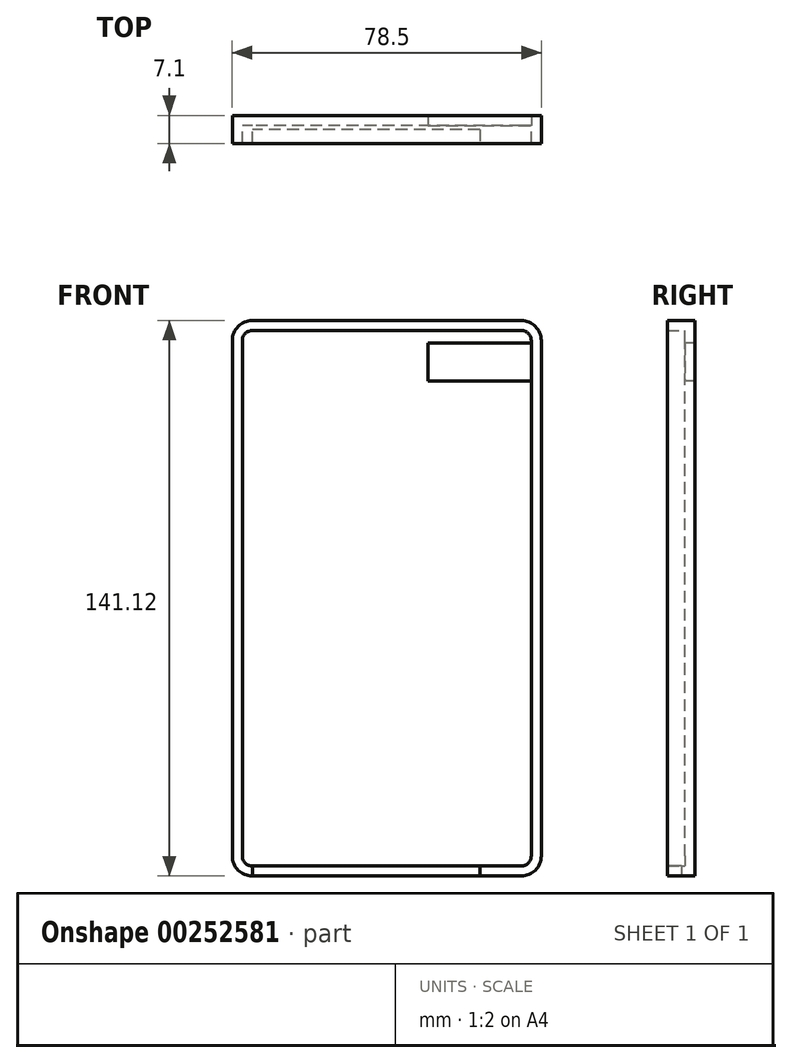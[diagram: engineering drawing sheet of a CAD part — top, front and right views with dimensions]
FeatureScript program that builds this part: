
annotation { "Feature Type Name" : "Feature", "Feature Type Description" : "" }
export const myFeature = defineFeature(function(context is Context, id is Id, definition is map)
    precondition{}
    {
        {
            var Q0;
            Q0=qCreatedBy(makeId("Front.planeOp"),FACE);
            var sketch = newSketch(context, id + "F0", { "sketchPlane" : qUnion([Q0])});
            skLineSegment(sketch, "E0.bottom", {"start": v(39.25, -70.56) * mm, "end": v(-39.25, -70.56) * mm});
            skLineSegment(sketch, "E0.top", {"start": v(39.25, 70.56) * mm, "end": v(-39.25, 70.56) * mm});
            skLineSegment(sketch, "E0.left", {"start": v(39.25, -70.56) * mm, "end": v(39.25, 70.56) * mm});
            skLineSegment(sketch, "E0.right", {"start": v(-39.25, -70.56) * mm, "end": v(-39.25, 70.56) * mm});
            skPoint(sketch, "E0.middle", {"position": v(0, 0) * mm});
            skSolve(sketch);
        }
        {
            var Q0;
            Q0 = qSketchRegion(id + "F0", true);
            extrude(context, id + "F1", {"entities" : qUnion([Q0]), "depth" : 7.1 * mm});
        }
        {
            var Q0;
            Q0=makeQuery(id+"F1.opExtrude","SWEPT_EDGE",EDGE,{"disambiguationData":[OSD([sQuery(id+"F0.wireOp",EDGE,"E0.top"),sQuery(id+"F0.wireOp",EDGE,"E0.right")])]});
            var Q1;
            Q1=makeQuery(id+"F1.opExtrude","SWEPT_EDGE",EDGE,{"disambiguationData":[OSD([sQuery(id+"F0.wireOp",EDGE,"E0.bottom"),sQuery(id+"F0.wireOp",EDGE,"E0.right")])]});
            var Q2;
            Q2=makeQuery(id+"F1.opExtrude","SWEPT_EDGE",EDGE,{"disambiguationData":[OSD([sQuery(id+"F0.wireOp",EDGE,"E0.bottom"),sQuery(id+"F0.wireOp",EDGE,"E0.left")])]});
            var Q3;
            Q3=makeQuery(id+"F1.opExtrude","SWEPT_EDGE",EDGE,{"disambiguationData":[OSD([sQuery(id+"F0.wireOp",EDGE,"E0.top"),sQuery(id+"F0.wireOp",EDGE,"E0.left")])]});
            fillet(context, id + "F2", {"entities" : qUnion([Q0, Q1, Q2, Q3]), "radius" : 5.08 * mm, "tangentPropagation" : true, "allowEdgeOverflow" : false});
        }
        {
            var Q0;
            Q0=makeQuery(id+"F1.opExtrude","CAP_FACE",FACE,{"disambiguationData":[OSD([sQuery(id+"F0.wireOp",EDGE,"E0.bottom"),sQuery(id+"F0.wireOp",EDGE,"E0.top"),sQuery(id+"F0.wireOp",EDGE,"E0.left"),sQuery(id+"F0.wireOp",EDGE,"E0.right")])],"isStart":false});
            shell(context, id + "F3", {"entities" : qUnion([Q0]), "thickness" : 2.54 * mm});
        }
        {
            var Q0;
            Q0=makeQuery(id+"F3.opShell","OFFSET_FACE",FACE,{"disambiguationData":[OSD([sQuery(id+"F0.wireOp",EDGE,"E0.bottom"),sQuery(id+"F0.wireOp",EDGE,"E0.top"),sQuery(id+"F0.wireOp",EDGE,"E0.left"),sQuery(id+"F0.wireOp",EDGE,"E0.right")])]});
            var sketch = newSketch(context, id + "F4", { "sketchPlane" : qUnion([Q0])});
            skLineSegment(sketch, "E1.bottom", {"start": v(10.5, 64.85) * mm, "end": v(36.7, 64.85) * mm});
            skLineSegment(sketch, "E1.top", {"start": v(10.5, 55.23) * mm, "end": v(36.7, 55.23) * mm});
            skLineSegment(sketch, "E1.left", {"start": v(10.5, 64.85) * mm, "end": v(10.5, 55.23) * mm});
            skLineSegment(sketch, "E1.right", {"start": v(36.7, 64.85) * mm, "end": v(36.7, 55.23) * mm});
            skSolve(sketch);
        }
        {
            var Q0;
            Q0=makeQuery(id+"F4.imprint","IMPRINT",FACE,{"disambiguationData":[TD([[makeQuery(id+"F4.imprint","IMPRINT",EDGE,{"derivedFrom":sQuery(id+"F4.wireOp",EDGE,"E1.bottom")}),-1.0]])]});
            extrude(context, id + "F5", {"entities" : qUnion([Q0]), "operationType" : NewBodyOperationType.REMOVE, "endBound" : BoundingType.SYMMETRIC, "oppositeDirection" : true, "depth" : 25.4 * mm});
        }
        {
            var Q0;
            Q0=makeQuery(id+"F1.opExtrude","SWEPT_FACE",FACE,{"disambiguationData":[OSD([sQuery(id+"F0.wireOp",EDGE,"E0.bottom")])]});
            var sketch = newSketch(context, id + "F6", { "sketchPlane" : qUnion([Q0])});
            skPoint(sketch, "E2.firstSnap0", {"position": v(34.17, 3.55) * mm});
            skLineSegment(sketch, "E2.bottom", {"start": v(19.39, 3.55) * mm, "end": v(-34.17, 3.55) * mm});
            skLineSegment(sketch, "E2.top", {"start": v(19.39, 7.1) * mm, "end": v(-34.17, 7.1) * mm});
            skLineSegment(sketch, "E2.left", {"start": v(19.39, 3.55) * mm, "end": v(19.39, 7.1) * mm});
            skLineSegment(sketch, "E2.right", {"start": v(-34.17, 3.55) * mm, "end": v(-34.17, 7.1) * mm});
            skLineSegment(sketch, "E3.bottom", {"start": v(23.65, 3.55) * mm, "end": v(-34.17, 3.55) * mm});
            skLineSegment(sketch, "E3.top", {"start": v(23.65, 7.1) * mm, "end": v(-34.17, 7.1) * mm});
            skLineSegment(sketch, "E3.left", {"start": v(23.65, 3.55) * mm, "end": v(23.65, 7.1) * mm});
            skSolve(sketch);
        }
        {
            var Q0;
            Q0 = qSketchRegion(id + "F6", true);
            extrude(context, id + "F7", {"entities" : qUnion([Q0]), "operationType" : NewBodyOperationType.REMOVE, "endBound" : BoundingType.SYMMETRIC, "oppositeDirection" : true, "depth" : 25.4 * mm});
        }
    });
